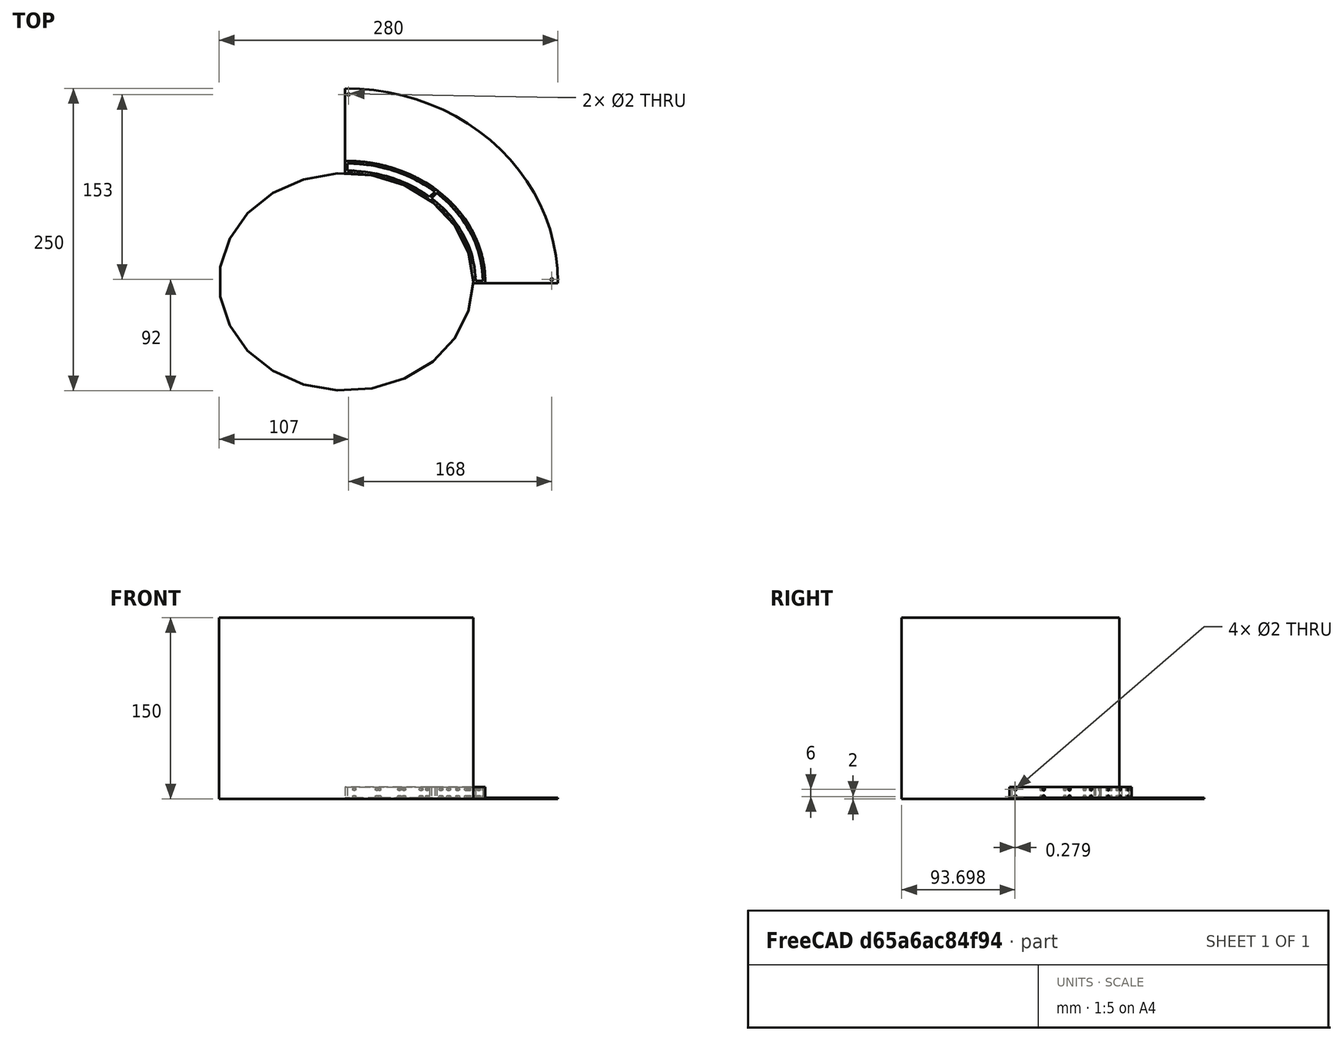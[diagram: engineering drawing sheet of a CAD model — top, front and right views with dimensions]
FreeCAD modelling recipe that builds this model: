
FCSTD DOCUMENT  (FreeCAD 0.14R3702 (Git))
Label: sun-hat
License: CC-BY 3.0
LicenseURL: http://creativecommons.org/licenses/by/3.0/
objects: Part::Feature×41, Part::Fuse×31, Part::Cut×15, Part::Extrusion×7, Part::Ellipse×5, Part::Cylinder×4, Part::Box×2, App::DocumentObjectGroup×1, Part::MultiCommon×1
note: 106 computed .brp shape members not serialized (recipe doc carries the construction recipe); baked Part::Feature solids carry a one-line shape summary decoded from their .brp

FEATURE [Part::Ellipse] Ellipse
  Angle0 = 0
  Angle1 = 360
  MajorRadius = 105
  MinorRadius = 90
FEATURE [Part::Ellipse] Ellipse001
  Angle0 = 0
  Angle1 = 360
  MajorRadius = 107
  MinorRadius = 92
FEATURE [Part::Ellipse] Ellipse002
  Angle0 = 0
  Angle1 = 360
  MajorRadius = 113
  MinorRadius = 98
FEATURE [Part::Ellipse] Ellipse003
  Angle0 = 0
  Angle1 = 360
  MajorRadius = 115
  MinorRadius = 100
FEATURE [Part::Feature] Face
  shape: bbox 210 x 180 x 2e-07 mm, 1 faces, 0 solids (baked)
FEATURE [Part::Feature] Face001
  shape: bbox 214 x 184 x 2e-07 mm, 1 faces, 0 solids (baked)
FEATURE [Part::Feature] Face002
  shape: bbox 226 x 196 x 2e-07 mm, 1 faces, 0 solids (baked)
FEATURE [Part::Feature] Face003
  shape: bbox 230 x 200 x 2e-07 mm, 1 faces, 0 solids (baked)
FEATURE [Part::Extrusion] Extrude
  Base = -> Face001
  Dir = (0,0,20)
  Placement = pos=(0,0,-1) rot=(0,0,1;0rad)
  Solid = false
FEATURE [Part::Extrusion] Extrude001
  Base = -> Face002
  Dir = (0,0,18)
  Solid = false
FEATURE [Part::Cut] Cut
  Base = -> Extrude001
  Tool = -> Extrude
FEATURE [Part::Box] Box  label="Cube"
  Height = 30
  Length = 2
  Placement = pos=(-1,0,-1) rot=(0,0,1;0rad)
  Width = 150
FEATURE [Part::Feature] Box001
  Placement = pos=(-0.707107,-0.707107,-1) rot=(0,0,1;0.785398rad)
  shape: bbox 107.5 x 107.5 x 30 mm, 6 faces (baked)
FEATURE [Part::Feature] Box002
  Placement = pos=(0,-1,-1) rot=(0,0,1;1.5708rad)
  shape: bbox 150 x 2 x 30 mm, 6 faces (baked)
FEATURE [Part::Feature] Box003
  Placement = pos=(0.707107,-0.707107,-1) rot=(0,0,1;2.35619rad)
  shape: bbox 107.5 x 107.5 x 30 mm, 6 faces (baked)
FEATURE [Part::Feature] Box004
  Placement = pos=(1,0,-1) rot=(0,0,1;3.14159rad)
  shape: bbox 2 x 150 x 30 mm, 6 faces (baked)
FEATURE [Part::Feature] Box005
  Placement = pos=(0.707107,0.707107,-1) rot=(0,0,1;3.92699rad)
  shape: bbox 107.5 x 107.5 x 30 mm, 6 faces (baked)
FEATURE [Part::Feature] Box006
  Placement = pos=(0,1,-1) rot=(0,0,-1;1.5708rad)
  shape: bbox 150 x 2 x 30 mm, 6 faces (baked)
FEATURE [Part::Feature] Box007
  Placement = pos=(-0.707107,0.707107,-1) rot=(0,0,-1;0.785398rad)
  shape: bbox 107.5 x 107.5 x 30 mm, 6 faces (baked)
FEATURE [Part::Cut] Cut001
  Base = -> Cut
  Tool = -> Box
FEATURE [Part::Cut] Cut002
  Base = -> Cut001
  Tool = -> Box007
FEATURE [Part::Cut] Cut003
  Base = -> Cut002
  Tool = -> Box006
FEATURE [Part::Cut] Cut004
  Base = -> Cut003
  Tool = -> Box005
FEATURE [Part::Cut] Cut005
  Base = -> Cut004
  Tool = -> Box004
FEATURE [Part::Cut] Cut006
  Base = -> Cut005
  Tool = -> Box003
FEATURE [Part::Cut] Cut007
  Base = -> Cut006
  Tool = -> Box002
FEATURE [Part::Cut] Cut008
  Base = -> Cut007
  Placement = pos=(0,0,-1) rot=(0,0,1;0rad)
  Tool = -> Box001
FEATURE [Part::Extrusion] Extrude002
  Base = -> Face
  Dir = (0,0,150)
  Placement = pos=(0,0,-1) rot=(0,0,1;0rad)
  Solid = false
FEATURE [Part::Extrusion] Extrude003
  Base = -> Face003
  Dir = (0,0,10)
  Solid = false
FEATURE [Part::Extrusion] Extrude004  label="central ellipse"
  Base = -> Face
  Dir = (0,0,150)
  Solid = false
FEATURE [Part::Cut] Cut009
  Base = -> Extrude003
  Tool = -> Extrude002
FEATURE [Part::Cut] Cut010  label="brim-1"
  Base = -> Cut009
  Tool = -> Cut008
FEATURE [Part::Cylinder] Cylinder
  Angle = 360
  Height = 150
  Placement = pos=(0,0,8) rot=(0,1,0;1.5708rad)
  Radius = 1
FEATURE [Part::Cylinder] Cylinder001
  Angle = 360
  Height = 150
  Placement = pos=(0,0,2) rot=(0,1,0;1.5708rad)
  Radius = 1
FEATURE [Part::Fuse] Fusion
  Base = -> Cylinder
  Placement = pos=(0,0,0) rot=(0,0,1;0.034907rad)
  Tool = -> Cylinder001
FEATURE [Part::Feature] Fusion001
  Placement = pos=(0,0,0) rot=(0,0,1;0.244346rad)
  shape: bbox 146 x 38.23 x 8 mm, 6 faces, 2 solids (baked)
FEATURE [Part::Feature] Fusion002
  Placement = pos=(0,0,0) rot=(0,0,1;0.453786rad)
  shape: bbox 135.7 x 67.55 x 8 mm, 6 faces, 2 solids (baked)
FEATURE [Part::Feature] Fusion003
  Placement = pos=(0,0,0) rot=(0,0,1;0.663225rad)
  shape: bbox 119.4 x 93.93 x 8 mm, 6 faces, 2 solids (baked)
FEATURE [Part::Feature] Fusion004
  Placement = pos=(0,0,0) rot=(0,0,1;0.872665rad)
  shape: bbox 97.95 x 116.2 x 8 mm, 6 faces, 2 solids (baked)
FEATURE [Part::Feature] Fusion005
  Placement = pos=(0,0,0) rot=(0,0,1;1.0821rad)
  shape: bbox 72.19 x 133.4 x 8 mm, 6 faces, 2 solids (baked)
FEATURE [Part::Feature] Fusion006
  Placement = pos=(0,0,0) rot=(0,0,1;1.29154rad)
  shape: bbox 43.27 x 144.7 x 8 mm, 6 faces, 2 solids (baked)
FEATURE [Part::Feature] Fusion007
  Placement = pos=(0,0,0) rot=(0,0,1;1.50098rad)
  shape: bbox 12.46 x 149.8 x 8 mm, 6 faces, 2 solids (baked)
FEATURE [Part::Feature] Fusion008
  Placement = pos=(0,0,0) rot=(0,0,1;1.71042rad)
  shape: bbox 22.86 x 148.8 x 8 mm, 6 faces, 2 solids (baked)
FEATURE [Part::Feature] Fusion009
  Placement = pos=(0,0,0) rot=(0,0,1;1.91986rad)
  shape: bbox 53.18 x 141.6 x 8 mm, 6 faces, 2 solids (baked)
FEATURE [Part::Feature] Fusion010
  Placement = pos=(0,0,0) rot=(0,0,1;2.1293rad)
  shape: bbox 81.18 x 128.3 x 8 mm, 6 faces, 2 solids (baked)
FEATURE [Part::Feature] Fusion011
  Placement = pos=(0,0,0) rot=(0,0,1;2.33874rad)
  shape: bbox 105.6 x 109.3 x 8 mm, 6 faces, 2 solids (baked)
FEATURE [Part::Feature] Fusion012
  Placement = pos=(0,0,0) rot=(0,0,1;2.54818rad)
  shape: bbox 125.5 x 85.54 x 8 mm, 6 faces, 2 solids (baked)
FEATURE [Part::Feature] Fusion013
  Placement = pos=(0,0,0) rot=(0,0,1;2.75762rad)
  shape: bbox 139.8 x 58.05 x 8 mm, 6 faces, 2 solids (baked)
FEATURE [Part::Feature] Fusion014
  Placement = pos=(0,0,0) rot=(0,0,1;2.96706rad)
  shape: bbox 148.1 x 28.02 x 8 mm, 6 faces, 2 solids (baked)
FEATURE [Part::Feature] Fusion015
  Placement = pos=(0,0,0) rot=(0,0,1;3.1765rad)
  shape: bbox 150 x 7.234 x 8 mm, 6 faces, 2 solids (baked)
FEATURE [Part::Feature] Fusion016
  Placement = pos=(0,0,0) rot=(0,0,1;3.38594rad)
  shape: bbox 146 x 38.23 x 8 mm, 6 faces, 2 solids (baked)
FEATURE [Part::Feature] Fusion017
  Placement = pos=(0,0,0) rot=(0,0,1;3.59538rad)
  shape: bbox 135.7 x 67.55 x 8 mm, 6 faces, 2 solids (baked)
FEATURE [Part::Feature] Fusion018
  Placement = pos=(0,0,0) rot=(0,0,1;3.80482rad)
  shape: bbox 119.4 x 93.93 x 8 mm, 6 faces, 2 solids (baked)
FEATURE [Part::Feature] Fusion019
  Placement = pos=(0,0,0) rot=(0,0,1;4.01426rad)
  shape: bbox 97.95 x 116.2 x 8 mm, 6 faces, 2 solids (baked)
FEATURE [Part::Feature] Fusion020
  Placement = pos=(0,0,0) rot=(0,0,-1;2.05949rad)
  shape: bbox 72.19 x 133.4 x 8 mm, 6 faces, 2 solids (baked)
FEATURE [Part::Feature] Fusion021
  Placement = pos=(0,0,0) rot=(0,0,-1;1.85005rad)
  shape: bbox 43.27 x 144.7 x 8 mm, 6 faces, 2 solids (baked)
FEATURE [Part::Feature] Fusion022
  Placement = pos=(0,0,0) rot=(0,0,-1;1.64061rad)
  shape: bbox 12.46 x 149.8 x 8 mm, 6 faces, 2 solids (baked)
FEATURE [Part::Feature] Fusion023
  Placement = pos=(0,0,0) rot=(0,0,-1;1.43117rad)
  shape: bbox 22.86 x 148.8 x 8 mm, 6 faces, 2 solids (baked)
FEATURE [Part::Feature] Fusion024
  Placement = pos=(0,0,0) rot=(0,0,-1;1.22173rad)
  shape: bbox 53.18 x 141.6 x 8 mm, 6 faces, 2 solids (baked)
FEATURE [Part::Feature] Fusion025
  Placement = pos=(0,0,0) rot=(0,0,-1;1.01229rad)
  shape: bbox 81.18 x 128.3 x 8 mm, 6 faces, 2 solids (baked)
FEATURE [Part::Feature] Fusion026
  Placement = pos=(0,0,0) rot=(0,0,-1;0.802851rad)
  shape: bbox 105.6 x 109.3 x 8 mm, 6 faces, 2 solids (baked)
FEATURE [Part::Feature] Fusion027
  Placement = pos=(0,0,0) rot=(0,0,-1;0.593412rad)
  shape: bbox 125.5 x 85.54 x 8 mm, 6 faces, 2 solids (baked)
FEATURE [Part::Feature] Fusion028
  Placement = pos=(0,0,0) rot=(0,0,-1;0.383972rad)
  shape: bbox 139.8 x 58.05 x 8 mm, 6 faces, 2 solids (baked)
FEATURE [Part::Feature] Fusion029
  Placement = pos=(0,0,0) rot=(0,0,-1;0.174533rad)
  shape: bbox 148.1 x 28.02 x 8 mm, 6 faces, 2 solids (baked)
FEATURE [Part::Fuse] Fusion030
  Base = -> Fusion
  Tool = -> Fusion001
FEATURE [Part::Fuse] Fusion031
  Base = -> Fusion029
  Tool = -> Fusion030
FEATURE [Part::Fuse] Fusion032
  Base = -> Fusion028
  Tool = -> Fusion031
FEATURE [Part::Fuse] Fusion033
  Base = -> Fusion027
  Tool = -> Fusion032
FEATURE [Part::Fuse] Fusion034
  Base = -> Fusion026
  Tool = -> Fusion033
FEATURE [Part::Fuse] Fusion035
  Base = -> Fusion025
  Tool = -> Fusion034
FEATURE [Part::Fuse] Fusion036
  Base = -> Fusion024
  Tool = -> Fusion035
FEATURE [Part::Fuse] Fusion037
  Base = -> Fusion023
  Tool = -> Fusion036
FEATURE [Part::Fuse] Fusion038
  Base = -> Fusion022
  Tool = -> Fusion037
FEATURE [Part::Fuse] Fusion039
  Base = -> Fusion021
  Tool = -> Fusion038
FEATURE [Part::Fuse] Fusion040
  Base = -> Fusion020
  Tool = -> Fusion039
FEATURE [Part::Fuse] Fusion041
  Base = -> Fusion019
  Tool = -> Fusion040
FEATURE [Part::Fuse] Fusion042
  Base = -> Fusion018
  Tool = -> Fusion041
FEATURE [Part::Fuse] Fusion043
  Base = -> Fusion017
  Tool = -> Fusion042
FEATURE [Part::Fuse] Fusion044
  Base = -> Fusion016
  Tool = -> Fusion043
FEATURE [Part::Fuse] Fusion045
  Base = -> Fusion015
  Tool = -> Fusion044
FEATURE [Part::Fuse] Fusion046
  Base = -> Fusion014
  Tool = -> Fusion045
FEATURE [Part::Fuse] Fusion047
  Base = -> Fusion013
  Tool = -> Fusion046
FEATURE [Part::Fuse] Fusion048
  Base = -> Fusion012
  Tool = -> Fusion047
FEATURE [Part::Fuse] Fusion049
  Base = -> Fusion011
  Tool = -> Fusion048
FEATURE [Part::Fuse] Fusion050
  Base = -> Fusion010
  Tool = -> Fusion049
FEATURE [Part::Fuse] Fusion051
  Base = -> Fusion009
  Tool = -> Fusion050
FEATURE [Part::Fuse] Fusion052
  Base = -> Fusion008
  Tool = -> Fusion051
FEATURE [Part::Fuse] Fusion053
  Base = -> Fusion007
  Tool = -> Fusion052
FEATURE [Part::Fuse] Fusion054
  Base = -> Fusion006
  Tool = -> Fusion053
FEATURE [Part::Fuse] Fusion055
  Base = -> Fusion005
  Tool = -> Fusion054
FEATURE [Part::Fuse] Fusion056
  Base = -> Fusion004
  Tool = -> Fusion055
FEATURE [Part::Fuse] Fusion057
  Base = -> Fusion003
  Tool = -> Fusion056
FEATURE [Part::Fuse] Fusion058
  Base = -> Fusion002
  Tool = -> Fusion057
FEATURE [Part::Cut] Cut011  label="brim-2"
  Base = -> Cut010
  Tool = -> Fusion058
FEATURE [Part::Ellipse] Ellipse004
  Angle0 = 0
  Angle1 = 360
  MajorRadius = 175
  MinorRadius = 160
FEATURE [App::DocumentObjectGroup] Group  label="Construction"
  Group = -> [Ellipse,Ellipse001,Ellipse002,Ellipse003,Extrude004,Ellipse004]
FEATURE [Part::Feature] Face004
  shape: bbox 350 x 320 x 2e-07 mm, 1 faces, 0 solids (baked)
FEATURE [Part::Extrusion] Extrude005
  Base = -> Face004
  Dir = (0,0,1)
  Solid = false
FEATURE [Part::Extrusion] Extrude006
  Base = -> Face002
  Dir = (0,0,18)
  Placement = pos=(0,0,-1) rot=(0,0,1;0rad)
  Solid = false
FEATURE [Part::Cut] Cut012
  Base = -> Extrude005
  Tool = -> Extrude006
FEATURE [Part::Fuse] Fusion059
  Base = -> Cut011
  Tool = -> Cut012
FEATURE [Part::Box] Box008  label="Cube001"
  Height = 16
  Length = 200
  Placement = pos=(-1,-1,-1) rot=(0,0,1;0rad)
  Width = 200
FEATURE [Part::MultiCommon] Common
  Shapes = -> [Fusion059,Box008]
FEATURE [Part::Cylinder] Cylinder002
  Angle = 360
  Height = 10
  Placement = pos=(170,2,-1) rot=(0,0,1;0rad)
  Radius = 1
FEATURE [Part::Cylinder] Cylinder003
  Angle = 360
  Height = 10
  Placement = pos=(2,155,-1) rot=(0,0,1;0rad)
  Radius = 1
FEATURE [Part::Cut] Cut013
  Base = -> Common
  Tool = -> Cylinder002
FEATURE [Part::Cut] Cut014
  Base = -> Cut013
  Tool = -> Cylinder003
